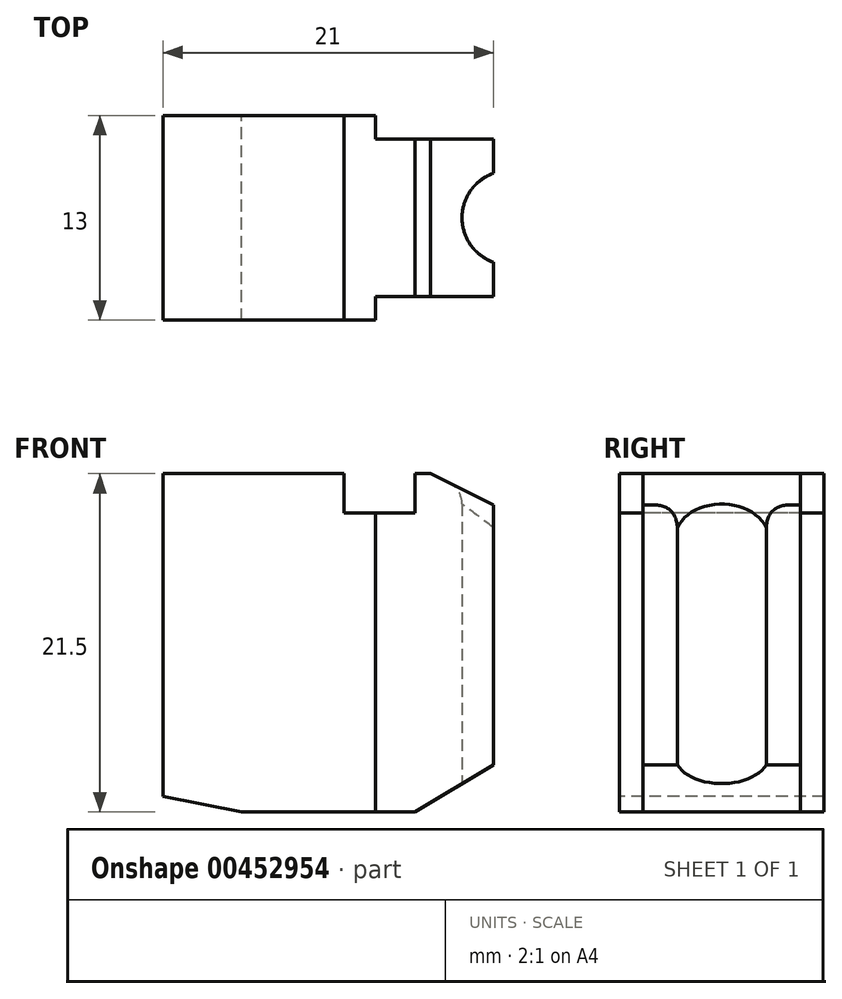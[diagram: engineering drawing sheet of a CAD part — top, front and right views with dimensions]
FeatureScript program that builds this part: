
annotation { "Feature Type Name" : "Feature", "Feature Type Description" : "" }
export const myFeature = defineFeature(function(context is Context, id is Id, definition is map)
    precondition{}
    {
        {
            var Q0;
            Q0=qCreatedBy(makeId("Top.planeOp"),FACE);
            var sketch = newSketch(context, id + "F0", { "sketchPlane" : qUnion([Q0])});
            skLineSegment(sketch, "E0", {"start": v(-13.5, 0) * mm, "end": v(-13.5, 6.5) * mm});
            skLineSegment(sketch, "E1", {"start": v(-13.5, 6.5) * mm, "end": v(0, 6.5) * mm});
            skLineSegment(sketch, "E2", {"start": v(0, 5) * mm, "end": v(7.5, 5) * mm});
            skLineSegment(sketch, "E3", {"start": v(7.5, 5) * mm, "end": v(7.5, 2.83) * mm});
            skLineSegment(sketch, "E4", {"start": v(0, 6.5) * mm, "end": v(0, 5) * mm});
            skLineSegment(sketch, "E5.MirrorCS", {"start": v(0, -6.5) * mm, "end": v(0, -5) * mm});
            skLineSegment(sketch, "E6.MirrorCS", {"start": v(7.5, -5) * mm, "end": v(7.5, -2.83) * mm});
            skLineSegment(sketch, "E7.MirrorCS", {"start": v(-13.5, -6.5) * mm, "end": v(0, -6.5) * mm});
            skLineSegment(sketch, "E8.MirrorCS", {"start": v(0, -5) * mm, "end": v(7.5, -5) * mm});
            skLineSegment(sketch, "E9.MirrorCS", {"start": v(-13.5, 0) * mm, "end": v(-13.5, -6.5) * mm});
            skArc(sketch, "E10", {"start": v(7.5, 2.83) * mm, "mid": v(5.5, 0) * mm, "end": v(7.5, -2.83) * mm});
            skSolve(sketch);
        }
        {
            var Q0;
            Q0 = qSketchRegion(id + "F0", true);
            extrude(context, id + "F1", {"entities" : qUnion([Q0]), "depth" : 21.5 * mm, "offsetDistance" : 25 * mm});
        }
        {
            var Q0;
            Q0=makeQuery(id+"F1.opExtrude","CAP_EDGE",EDGE,{"disambiguationData":[OSD([sQuery(id+"F0.wireOp",EDGE,"E6.MirrorCS")])],"isStart":false});
            chamfer(context, id + "F2", {"entities" : qUnion([Q0]), "chamferType" : ChamferType.TWO_OFFSETS, "width1" : 4 * mm, "oppositeDirection" : false, "width2" : 2 * mm, "tangentPropagation" : true});
        }
        {
            var Q0;
            Q0=makeQuery(id+"F1.opExtrude","CAP_FACE",FACE,{"disambiguationData":[OSD([sQuery(id+"F0.wireOp",EDGE,"E0"),sQuery(id+"F0.wireOp",EDGE,"E1"),sQuery(id+"F0.wireOp",EDGE,"E2"),sQuery(id+"F0.wireOp",EDGE,"E3"),sQuery(id+"F0.wireOp",EDGE,"E4"),sQuery(id+"F0.wireOp",EDGE,"E5.MirrorCS"),sQuery(id+"F0.wireOp",EDGE,"E6.MirrorCS"),sQuery(id+"F0.wireOp",EDGE,"E7.MirrorCS"),sQuery(id+"F0.wireOp",EDGE,"E8.MirrorCS"),sQuery(id+"F0.wireOp",EDGE,"E9.MirrorCS"),sQuery(id+"F0.wireOp",EDGE,"E10")])],"isStart":false});
            var sketch = newSketch(context, id + "F3", { "sketchPlane" : qUnion([Q0])});
            skLineSegment(sketch, "E11", {"start": v(-2, 6.5) * mm, "end": v(-2, -6.5) * mm});
            skLineSegment(sketch, "E12", {"start": v(2.5, 5) * mm, "end": v(2.5, -5) * mm});
            skLineSegment(sketch, "E13", {"start": v(-2, 6.5) * mm, "end": v(0, 6.5) * mm});
            skLineSegment(sketch, "E14", {"start": v(0, 6.5) * mm, "end": v(0, 5) * mm});
            skLineSegment(sketch, "E15", {"start": v(0, 5) * mm, "end": v(2.5, 5) * mm});
            skLineSegment(sketch, "E16.MirrorCS", {"start": v(0, -5) * mm, "end": v(2.5, -5) * mm});
            skLineSegment(sketch, "E17.MirrorCS", {"start": v(0, -6.5) * mm, "end": v(0, -5) * mm});
            skLineSegment(sketch, "E18.MirrorCS", {"start": v(-2, -6.5) * mm, "end": v(0, -6.5) * mm});
            skSolve(sketch);
        }
        {
            var Q0;
            Q0 = qSketchRegion(id + "F3", true);
            extrude(context, id + "F4", {"entities" : qUnion([Q0]), "operationType" : NewBodyOperationType.REMOVE, "oppositeDirection" : true, "depth" : 2.5 * mm, "offsetDistance" : 25 * mm});
        }
        {
            var Q0;
            Q0=makeQuery(id+"F1.opExtrude","CAP_EDGE",EDGE,{"disambiguationData":[OSD([sQuery(id+"F0.wireOp",EDGE,"E0"),sQuery(id+"F0.wireOp",EDGE,"E9.MirrorCS")])],"isStart":true});
            chamfer(context, id + "F5", {"entities" : qUnion([Q0]), "chamferType" : ChamferType.TWO_OFFSETS, "width1" : 1 * mm, "oppositeDirection" : true, "width2" : 5 * mm, "tangentPropagation" : true});
        }
        {
            var Q0;
            Q0=makeQuery(id+"F1.opExtrude","CAP_EDGE",EDGE,{"disambiguationData":[OSD([sQuery(id+"F0.wireOp",EDGE,"E6.MirrorCS")])],"isStart":true});
            chamfer(context, id + "F6", {"entities" : qUnion([Q0]), "chamferType" : ChamferType.TWO_OFFSETS, "width1" : 3 * mm, "oppositeDirection" : true, "width2" : 5 * mm, "tangentPropagation" : true});
        }
        {
            var Q0;
            Q0=makeQuery(id+"F2.opChamfer","BLEND_EDGE",EDGE,{"blendedFrom":[makeQuery(id+"F1.opExtrude","CAP_EDGE",EDGE,{"disambiguationData":[OSD([sQuery(id+"F0.wireOp",EDGE,"E6.MirrorCS")])],"isStart":false}),makeQuery(id+"F1.opExtrude","SWEPT_FACE",FACE,{"disambiguationData":[OSD([sQuery(id+"F0.wireOp",EDGE,"E10")])]})],"blendedInto":[makeQuery(id+"F1.opExtrude","SWEPT_FACE",FACE,{"disambiguationData":[OSD([sQuery(id+"F0.wireOp",EDGE,"E10")])]})]});
            fillet(context, id + "F7", {"entities" : qUnion([Q0]), "tangentPropagation" : true, "radius" : 1.5 * mm, "defaultsChanged" : true, "vertexSettings" : [], "allowEdgeOverflow" : false});
        }
    });
